# Revit family: 4LRS24836B75FTT-B.V3,B2FTT-B.V3
name_source: partatom
category: Plumbing Fixtures
units: mm (PartAtom-declared; Revit-internal decimal feet)

## family parameters
Always vertical = Yes
Cut with Voids When Loaded = No
OmniClass Number = 23.45.05.14.17
OmniClass Title = Showers
Part Type = Normal
Room Calculation Point = No
Round Connector Dimension = Use Diameter
Shared = No
Work Plane-Based = No

## types (4) — shared parameters
Assembly Code = D2010710
Description = Trench Drain Pan, Real Tile, Beveled Threshold
Keynote = 22 40 00.B3
Manufacturer = Best Bath Systems, Inc.
Type Comments = Barrier Free
URL = http://www.bestbath.com
Unit Depth = 37"
Unit Width = 48"

## per-type parameters (varying)
| type | Pan Height | Threshold Height | Unit Height |
| 4LRS24836B75FTB.V3 | 5 3/4" | 3/4" | 81 1/4" |
| 4LRS24836B2FTB.V3 | 7" | 2" | 82 1/2" |
| 4LRS24836B75FTT.V3 | 5 3/4" | 3/4" | 81 1/4" |
| 4LRS24836B2FTT.V3 | 7" | 2" | 82 1/2" |

note: column(s) folded — value = type name in every type: Model

## geometry (parser evidence)
native form markers: Blend x10, Sweep x2
no freeform markers — native parametric forms only
